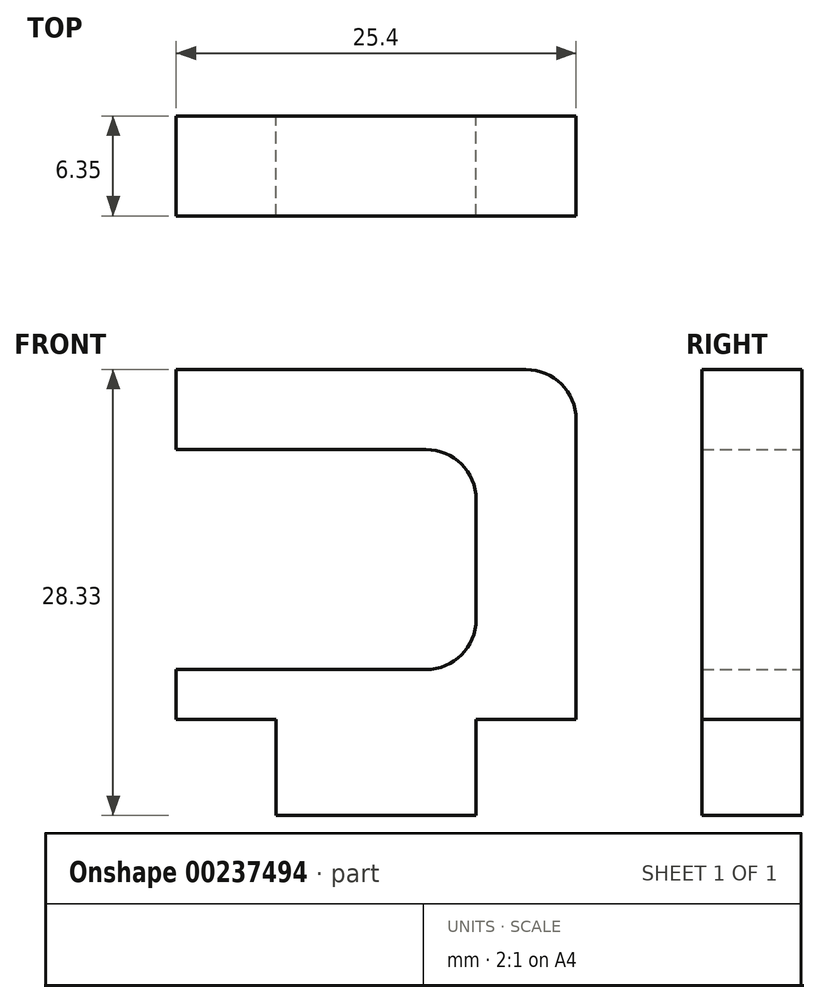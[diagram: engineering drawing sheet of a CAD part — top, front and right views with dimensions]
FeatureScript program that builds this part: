
annotation { "Feature Type Name" : "Feature", "Feature Type Description" : "" }
export const myFeature = defineFeature(function(context is Context, id is Id, definition is map)
    precondition{}
    {
        {
            var Q0;
            Q0=qCreatedBy(makeId("Front.planeOp"),FACE);
            var sketch = newSketch(context, id + "F0", { "sketchPlane" : qUnion([Q0])});
            skLineSegment(sketch, "E0.top", {"start": v(0, -6.1) * mm, "end": v(12.7, -6.1) * mm});
            skLineSegment(sketch, "E0.left", {"start": v(0, 0) * mm, "end": v(0, -6.1) * mm});
            skLineSegment(sketch, "E0.right", {"start": v(12.7, 0) * mm, "end": v(12.7, -6.1) * mm});
            skLineSegment(sketch, "E1.bottom", {"start": v(-6.35, 0) * mm, "end": v(0, 0) * mm});
            skLineSegment(sketch, "E1.top", {"start": v(-6.35, 3.17) * mm, "end": v(9.52, 3.17) * mm});
            skLineSegment(sketch, "E1.left", {"start": v(-6.35, 0) * mm, "end": v(-6.35, 3.17) * mm});
            skLineSegment(sketch, "E1.right", {"start": v(19.05, 0) * mm, "end": v(19.05, 3.17) * mm});
            skLineSegment(sketch, "E2", {"start": v(19.05, 3.17) * mm, "end": v(19.05, 19.05) * mm});
            skLineSegment(sketch, "E3", {"start": v(15.87, 22.22) * mm, "end": v(-6.35, 22.22) * mm});
            skLineSegment(sketch, "E4", {"start": v(-6.35, 22.22) * mm, "end": v(-6.35, 17.14) * mm});
            skLineSegment(sketch, "E5", {"start": v(-6.35, 17.14) * mm, "end": v(9.52, 17.14) * mm});
            skLineSegment(sketch, "E6", {"start": v(12.7, 13.97) * mm, "end": v(12.7, 6.35) * mm});
            skPoint(sketch, "E6.endSnap0", {"position": v(6.35, 3.17) * mm});
            skLineSegment(sketch, "E7.trimOffspring", {"start": v(12.7, 0) * mm, "end": v(19.05, 0) * mm});
            skPoint(sketch, "E8.visualSharp", {"position": v(12.7, 17.14) * mm});
            skArc(sketch, "E8.filletArc", {"start": v(12.7, 13.97) * mm, "mid": v(11.77, 16.22) * mm, "end": v(9.52, 17.14) * mm});
            skPoint(sketch, "E9.visualSharp", {"position": v(19.05, 22.22) * mm});
            skArc(sketch, "E9.filletArc", {"start": v(19.05, 19.05) * mm, "mid": v(18.12, 21.3) * mm, "end": v(15.87, 22.22) * mm});
            skPoint(sketch, "E10.visualSharp", {"position": v(12.7, 3.17) * mm});
            skArc(sketch, "E10.filletArc", {"start": v(9.52, 3.18) * mm, "mid": v(11.77, 4.1) * mm, "end": v(12.7, 6.35) * mm});
            skSolve(sketch);
        }
        {
            var Q0;
            Q0 = qSketchRegion(id + "F0", true);
            extrude(context, id + "F1", {"entities" : qUnion([Q0]), "depth" : 6.35 * mm});
        }
    });
